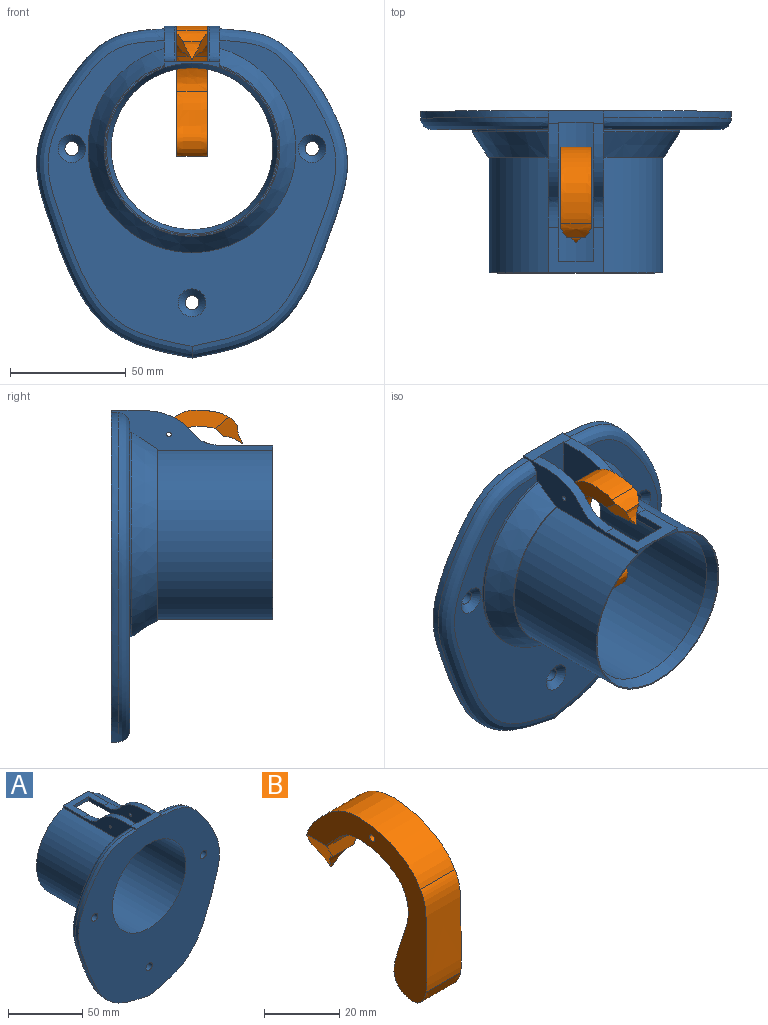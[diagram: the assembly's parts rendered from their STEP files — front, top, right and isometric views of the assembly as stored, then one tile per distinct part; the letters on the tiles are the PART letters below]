
ASSEMBLY  parts=2 mates=1
PART A: 31 faces, bbox 136.5x70.2x144.4 mm
  f0: cylinder r=1mm len=4.5mm, axis (-1,0,0), area 28.3mm2, adj f9,f30
  f1: extruded ~44.94x15.45mm, area 222.8mm2, adj f7,f9,f25,f30
  f2: cylinder r=37.5mm len=75mm, axis (0,-1,0), area 10559.5mm2, adj f4,f9,f11,f12
  f3: cylinder r=35mm len=70mm, axis (0,-1,0), area 13387.2mm2, adj f5,f26,f27,f28,f30
  f4: plane 75x75mm, normal (0,1,0), area 132.6mm2, adj f2,f9,f12,f25,f26
  f5: plane 143.42x136.29mm, normal (0,-1,0), area 11059.3mm2, adj f3,f7,f9,f12,f17,f18,f19,f22
  f6: cylinder r=1mm len=4.5mm, axis (-1,0,0), area 28.3mm2, adj f12,f28
  f7: plane 24x5.53mm, normal (0,0,1), area 124.7mm2, adj f1,f5,f8,f9,f12,f27,f28,f30
  f8: extruded ~44.94x15.45mm, area 222.8mm2, adj f7,f12,f25,f28
  f9: plane 70.19x17.8mm, normal (-1,0,0), area 459mm2, adj f0,f1,f2,f4,f5,f7,f10,f11
  f10: cone r=45mm half-angle=32.5deg, axis (0,-1,0), area 3080.7mm2, adj f9,f11,f12,f13
  f11: plane 76x74.06mm, normal (0,1,0), area 106.4mm2, adj f2,f9,f10,f12
  f12: plane 70.19x17.8mm, normal (1,0,0), area 459mm2, adj f2,f4,f5,f6,f7,f8,f10,f11
  f13: cylinder r=45mm len=90mm, axis (0,-1,0), area 258.4mm2, adj f9,f10,f12,f21
  f14: cone r=3mm half-angle=45deg, axis (0,1,0), area 120mm2, adj f17,f21
  f15: cone r=3mm half-angle=45deg, axis (0,1,0), area 120mm2, adj f18,f21
  f16: cone r=3mm half-angle=45deg, axis (0,1,0), area 120mm2, adj f19,f21
  f17: cylinder r=3mm len=6mm, axis (0,-1,0), area 94.2mm2, adj f5,f14
  f18: cylinder r=3mm len=6mm, axis (0,-1,0), area 94.2mm2, adj f5,f15
  f19: cylinder r=3mm len=6mm, axis (0,-1,0), area 94.2mm2, adj f5,f16
  f20: bspline ~143.04x70.44mm, area 1576.7mm2, adj f12,f21,f22,f23
  f21: plane 132.32x124.51mm, normal (0,1,0), area 6103.3mm2, adj f9,f12,f13,f14,f15,f16,f20,f23
  f22: extruded ~142.4x67.25mm, area 619.8mm2, adj f5,f12,f20,f24
  f23: bspline ~142.91x70.66mm, area 1576.4mm2, adj f9,f20,f21,f24
  f24: extruded ~142.4x67.25mm, area 619.8mm2, adj f5,f9,f22,f23
  f25: plane 24x19.54mm, normal (0,0,1), area 250.8mm2, adj f1,f4,f8,f9,f12,f28,f29,f30
  f26: cone r=37mm half-angle=21.8deg, axis (0,1,0), area 1218.1mm2, adj f3,f4,f29
  f27: plane 18.65x15mm, normal (0,1,0), area 271.5mm2, adj f3,f7,f28,f30
  f28: plane 60x18.96mm, normal (-1,0,0), area 622mm2, adj f3,f6,f7,f8,f25,f27,f29
  f29: plane 15x3.31mm, normal (0,-1,0), area 41.5mm2, adj f25,f26,f28,f30
  f30: plane 60x18.96mm, normal (1,0,0), area 622mm2, adj f0,f1,f3,f7,f25,f27,f29
PART B: 14 faces, bbox 13x46.2x50.4 mm
  f0: extruded ~17.37x13mm, area 272.5mm2, adj f1,f5,f6,f11,f12,f13
  f1: plane 12.53x4.47mm, normal (0,-1,0), area 44.4mm2, adj f0,f2,f12,f13
  f2: extruded ~7.94x6.19mm, area 37.4mm2, adj f1,f3,f12,f13
  f3: extruded ~7.94x7.47mm, area 36.7mm2, adj f2,f4,f12,f13
  f4: extruded ~13x7.38mm, area 86mm2, adj f3,f5,f7,f11,f12,f13
  f5: plane 50.4x45.58mm, normal (-1,0,0), area 632.1mm2, adj f0,f4,f6,f7,f8,f9,f10,f12
  f6: extruded ~13x12.72mm, area 211.6mm2, adj f0,f5,f10,f11
  f7: extruded ~41.7x13mm, area 660.9mm2, adj f4,f5,f8,f11
  f8: extruded ~32.36x13mm, area 426.8mm2, adj f5,f7,f10,f11
  f9: cylinder r=1mm len=13mm, axis (-1,0,0), area 81.7mm2, adj f5,f11
  f10: extruded ~33.06x13mm, area 600.5mm2, adj f5,f6,f8,f11
  f11: plane 50.4x45.58mm, normal (1,0,0), area 632.1mm2, adj f0,f4,f6,f7,f8,f9,f10,f13
  f12: extruded ~12.49x8.27mm, area 68.1mm2, adj f0,f1,f2,f3,f4,f5
  f13: extruded ~12.49x8.27mm, area 68.1mm2, adj f0,f1,f2,f3,f4,f11
PLACE A rot(axis=(0,0,1),180deg) t=(2.52,96.5,24.43)mm fixed
PLACE B rot(axis=(0,-0.34,-0.94),180deg) t=(2.52,61.21,54.67)mm
MATE revolute B.f9 <-> A.f0  axis (-1,0,0) through (-3.98,71.5,66.93)mm
